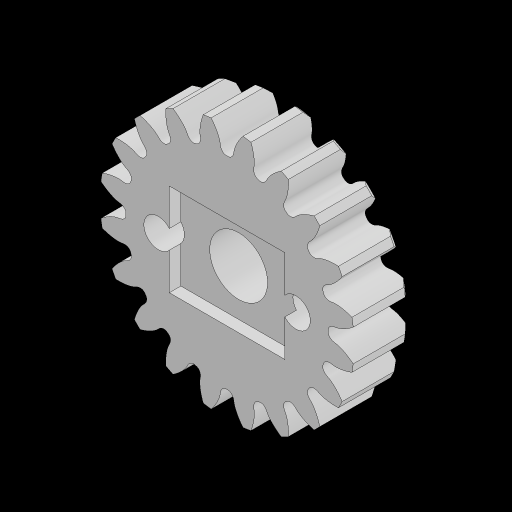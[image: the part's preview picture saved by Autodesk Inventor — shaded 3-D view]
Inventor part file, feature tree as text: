
AUTODESK INVENTOR PART (.ipt)
format: ipt  version: 2023.2 (Build 272271030, 271C)  size: 779,264 bytes
history: native  units: mm
features: sketch x5, extrude x3, hole x2, pattern_circular x1, revolve x1, projected_geometry x1
ambient origin geometry x8: Origin, YZ Plane, XZ Plane, XY Plane, X Axis, Y Axis, Z Axis, Center Point
bodies: Solid1 (feature_tree)
feature tree (13):
  sketch  "Sketch1"  dims[d0=5.0mm d1=0.0mm]
  extrude  "Extrusion1"  TaperAngle=0.0deg  [1 undecoded]
  extrude  "Extrusion2"  Depth=200.0mm TaperAngle=360.0deg
  pattern_circular  "Circular Pattern1"  [2 undecoded]
  hole  "Hole1"  [1 undecoded]
  hole  "Hole2"  [1 undecoded]
  revolve  "Revolution2"  Angle=90.0deg
  extrude  "Extrusion4"  Depth=10.0mm
  sketch  "Sketch2"  dims[d2=0.0mm d3=0.0mm d4=200.0mm d5=360.0deg]
  sketch  "Sketch3"  dims[d7=11.9mm]
  sketch  "Sketch6"  dims[d8=2.5mm d9=6.0mm d10=5.5mm d11=2.0mm d12=90.0deg d13=8.0mm d14=20.594885mm]
  projected_geometry  "Projected Loop2"
  sketch  "Sketch7"  dims[d15=5.0mm d16=6.0mm d17=6.0mm d18=2.0mm d19=90.0deg d20=8.0mm d21=20.594885mm d33=11.0mm d34=0.5mm d35=0.5mm d36=90.0deg d37=10.0mm d38=8.0mm d39=1.0mm d40=0.0mm]
note: 5 required parameter values undecoded (feature->parameter linkage not recoverable at this tier; creation-order binding heuristic only, values carry confidence <= 0.55)
